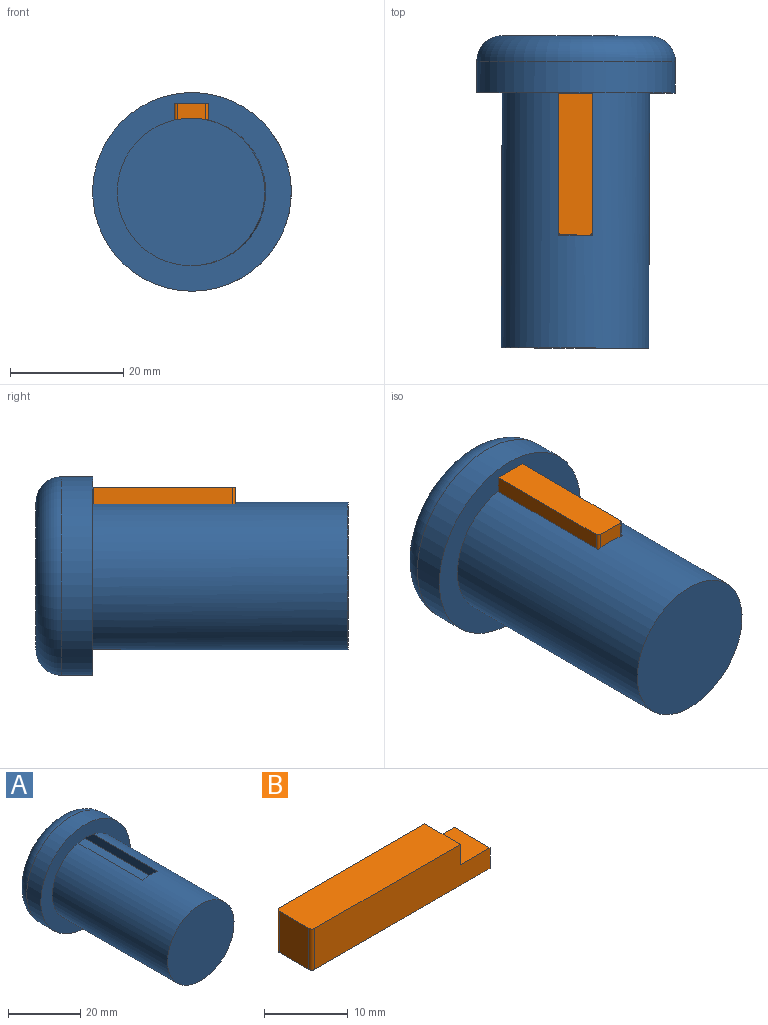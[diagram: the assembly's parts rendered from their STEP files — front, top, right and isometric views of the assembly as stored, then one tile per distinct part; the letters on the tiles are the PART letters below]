
ASSEMBLY  parts=2 mates=1
PART A: 12 faces, bbox 37.9x55x37.9 mm
  f0: plane 30.19x3mm, normal (1,0,0), area 90.6mm2, adj f2,f4,f7,f8,f10
  f1: plane 30.19x3mm, normal (-1,0,0), area 90.6mm2, adj f2,f4,f7,f8,f10
  f2: plane 30.19x6mm, normal (0,0,1), area 181.1mm2, adj f0,f1,f8,f10
  f3: plane 35x35mm, normal (0,-1,0), area 431.2mm2, adj f4,f5,f7
  f4: cylinder r=13mm len=6mm, axis (0,1,0), area 30.3mm2, adj f0,f1,f3,f8
  f5: cylinder r=17.5mm len=35mm, axis (0,1,0), area 604.8mm2, adj f3,f11
  f6: plane 26x26mm, normal (0,1,0), area 530.9mm2, adj f11
  f7: cylinder r=13mm len=45mm, axis (0,1,0), area 3523.1mm2, adj f0,f1,f3,f9,f10
  f8: plane 6x3.35mm, normal (0,-1,0), area 19.4mm2, adj f0,f1,f2,f4
  f9: plane 26x26mm, normal (0,-1,0), area 530.9mm2, adj f7
  f10: plane 6x3.35mm, normal (0,1,0), area 19.4mm2, adj f0,f1,f2,f7
  f11: torus R=13mm, axis (0,-1,0), area 704.6mm2, adj f5,f6
PART B: 10 faces, bbox 30x6x6 mm
  f0: plane 25x6mm, normal (0,0,1), area 149.9mm2, adj f1,f5,f6,f7,f8,f9
  f1: plane 6x5mm, normal (-1,0,0), area 30mm2, adj f0,f2,f8,f9
  f2: plane 30x6mm, normal (0,0,-1), area 179.9mm2, adj f1,f3,f6,f7,f8,f9
  f3: plane 6x3mm, normal (1,0,0), area 18mm2, adj f2,f4,f6,f7
  f4: plane 6x5mm, normal (0,0,1), area 30mm2, adj f3,f5,f6,f7
  f5: plane 6x3mm, normal (1,0,0), area 18mm2, adj f0,f4,f6,f7
  f6: plane 29.5x6mm, normal (0,-1,0), area 162mm2, adj f0,f2,f3,f4,f5,f9
  f7: plane 29.5x6mm, normal (0,1,0), area 162mm2, adj f0,f2,f3,f4,f5,f8
  f8: cylinder r=0.5mm len=6mm, axis (0,0,-1), area 4.7mm2, adj f0,f1,f2,f7
  f9: cylinder r=0.5mm len=6mm, axis (0,0,1), area 4.7mm2, adj f0,f1,f2,f6
PLACE A rot(axis=(0,0,-1),0.2deg) t=(10.39,78.19,14.66)mm
PLACE B rot(axis=(0,0,1),89.8deg) t=(10.26,43.09,30.31)mm
MATE fastened A.f2 <-> B.f2  axis (0,0,1) through (10.32,58.1,24.31)mm
